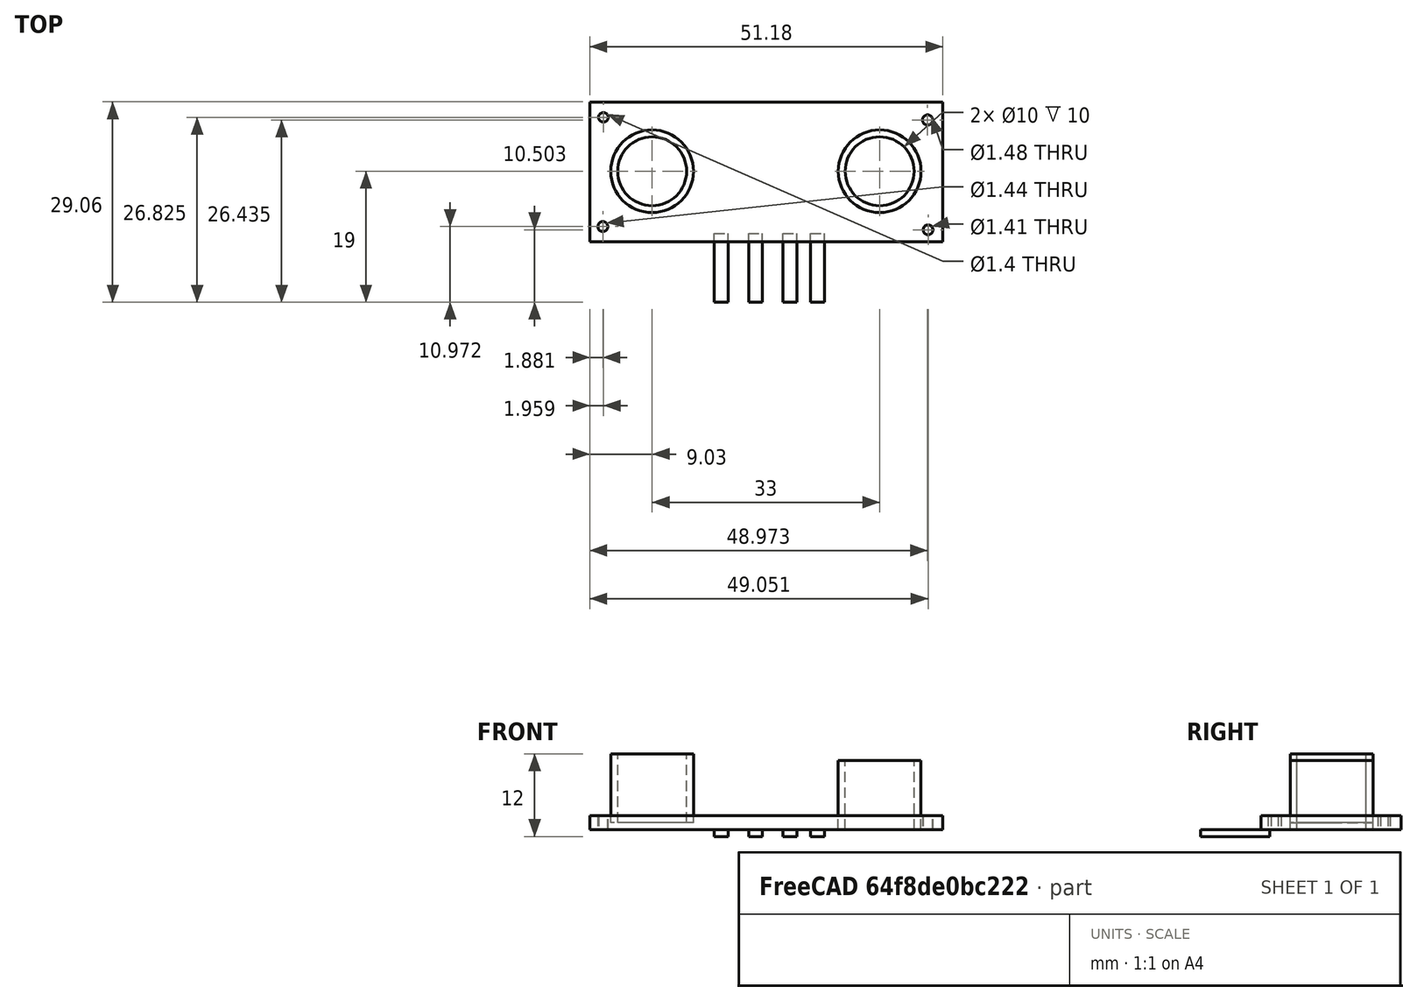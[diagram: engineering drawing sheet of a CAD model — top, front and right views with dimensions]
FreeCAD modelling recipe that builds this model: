
FCSTD DOCUMENT  (FreeCAD 0.19R24291 (Git))
Label: ultrasonidos
License: All rights reserved
LicenseURL: http://en.wikipedia.org/wiki/All_rights_reserved
objects: Part::Box×4, Part::FeaturePython×2, Sketcher::SketchObject×1, PartDesign::Pad×1, PartDesign::Body×1
note: 10 computed .brp shape members not serialized (recipe doc carries the construction recipe); baked Part::Feature solids carry a one-line shape summary decoded from their .brp

FEATURE [Sketcher::SketchObject] Sketch
  FullyConstrained = false
  MapMode = 5
  Support = -> [XY_Plane]
  sketch-geometry (8):
    g0: LineSegment StartX=-25.0348 StartY=11.057 StartZ=0 EndX=26.1474 EndY=11.057 EndZ=0
    g1: LineSegment StartX=26.1474 StartY=11.057 StartZ=0 EndX=26.1474 EndY=-9.24896 EndZ=0
    g2: LineSegment StartX=26.1474 StartY=-9.24896 StartZ=0 EndX=-25.0348 EndY=-9.24896 EndZ=0
    g3: LineSegment StartX=-25.0348 StartY=-9.24896 StartZ=0 EndX=-25.0348 EndY=11.057 EndZ=0
    g4: Circle CenterX=-23.0712 CenterY=8.82531 CenterZ=0 NormalX=0 NormalY=0 NormalZ=1 AngleXU=0 Radius=0.698514
    g5: Circle CenterX=23.9427 CenterY=8.43482 CenterZ=0 NormalX=0 NormalY=0 NormalZ=1 AngleXU=0 Radius=0.740892
    g6: Circle CenterX=24.0208 CenterY=-7.49681 CenterZ=0 NormalX=0 NormalY=0 NormalZ=1 AngleXU=0 Radius=0.707187
    g7: Circle CenterX=-23.1493 CenterY=-7.02823 CenterZ=0 NormalX=0 NormalY=0 NormalZ=1 AngleXU=0 Radius=0.720017
  constraints (8):
    c: Coincident(g0,g1)
    c: Coincident(g1,g2)
    c: Coincident(g2,g3)
    c: Coincident(g3,g0)
    c: Horizontal(g0)
    c: Horizontal(g2)
    c: Vertical(g1)
    c: Vertical(g3)
FEATURE [PartDesign::Pad] Pad
  Direction = (1,1,1)
  Length = 2
  Length2 = 100
  Profile = -> Sketch
  Type = 0
FEATURE [PartDesign::Body] Body
  Group = -> [Sketch,Pad]
  Origin = -> Origin
  Tip = -> Pad
FEATURE [Part::FeaturePython] Tube  label="cilindro1"  # WARN: FeaturePython — macro-defined, semantics opaque (R4)
  AttacherType = Attacher::AttachEngine3D
  Height = 10
  InnerRadius = 5
  OuterRadius = 6
  Placement = pos=(-16,1,1) rot=(0,0,1;0rad)
FEATURE [Part::FeaturePython] Tube001  label="Cilindro2"  # WARN: FeaturePython — macro-defined, semantics opaque (R4)
  AttacherType = Attacher::AttachEngine3D
  Height = 10
  InnerRadius = 5
  OuterRadius = 6
  Placement = pos=(17,1,0) rot=(0,0,1;0rad)
FEATURE [Part::Box] Box  label="contacto1"
  AttacherType = Attacher::AttachEngine3D
  Height = 1
  Length = 2
  Placement = pos=(-7,-18,-1) rot=(0,0,1;0rad)
  Width = 10
FEATURE [Part::Box] Box001  label="contacto2"
  AttacherType = Attacher::AttachEngine3D
  Height = 1
  Length = 2
  Placement = pos=(-2,-18,-1) rot=(0,0,1;0rad)
  Width = 10
FEATURE [Part::Box] Box002  label="contacto3"
  AttacherType = Attacher::AttachEngine3D
  Height = 1
  Length = 2
  Placement = pos=(3,-18,-1) rot=(0,0,1;0rad)
  Width = 10
FEATURE [Part::Box] Box003  label="contacto4"
  AttacherType = Attacher::AttachEngine3D
  Height = 1
  Length = 2
  Placement = pos=(7,-18,-1) rot=(0,0,1;0rad)
  Width = 10
